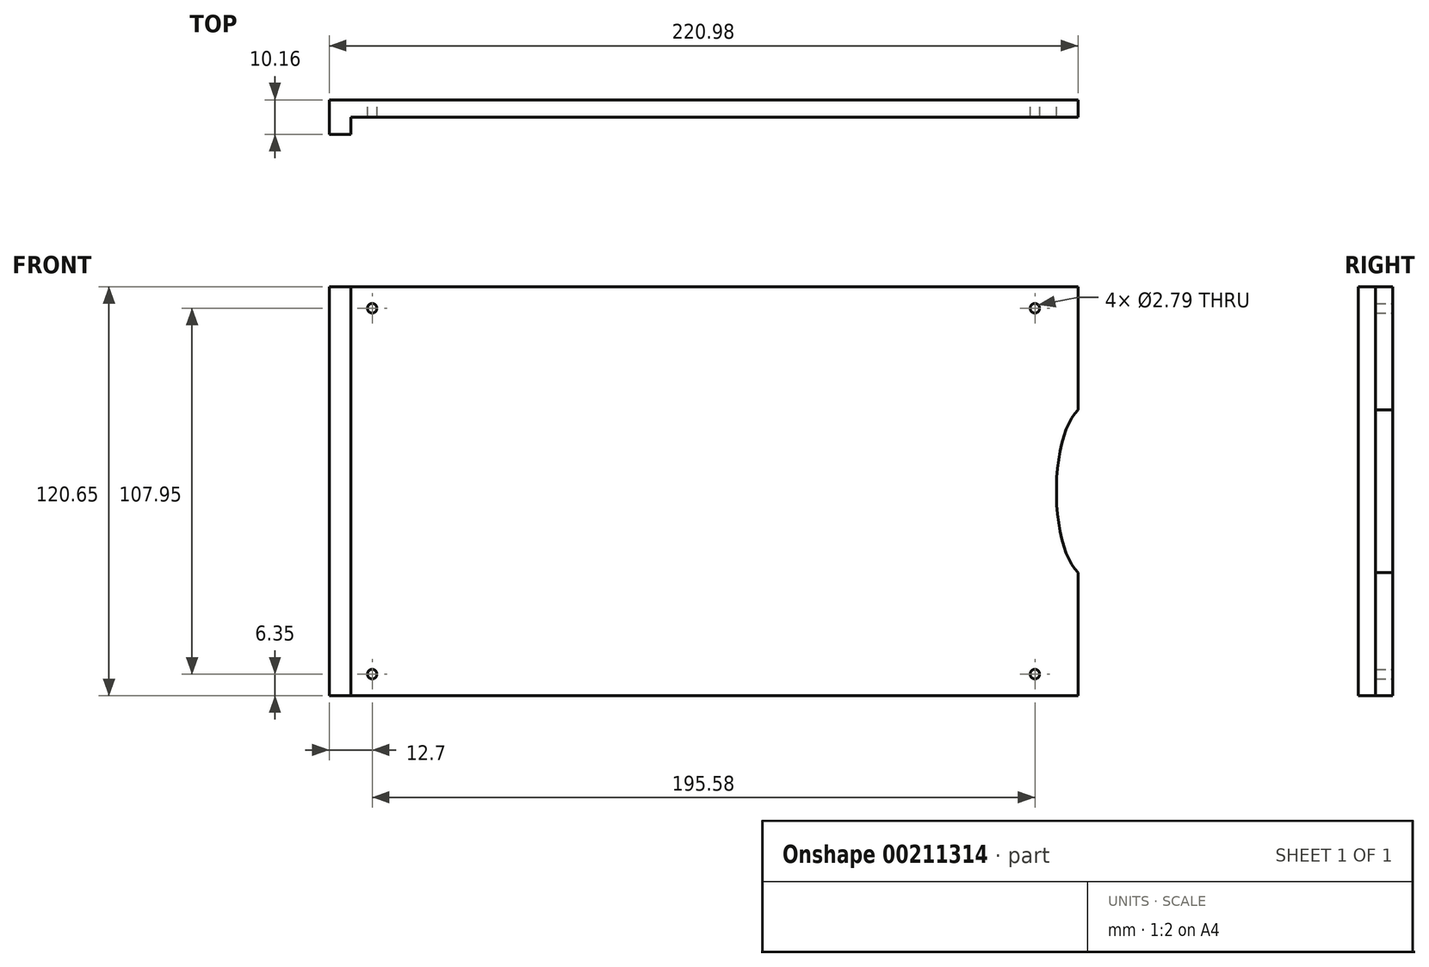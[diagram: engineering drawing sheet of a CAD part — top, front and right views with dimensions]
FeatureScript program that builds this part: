
annotation { "Feature Type Name" : "Feature", "Feature Type Description" : "" }
export const myFeature = defineFeature(function(context is Context, id is Id, definition is map)
    precondition{}
    {
        {
            var Q0;
            Q0=qCreatedBy(makeId("Front.planeOp"),FACE);
            var sketch = newSketch(context, id + "F0", { "sketchPlane" : qUnion([Q0])});
            skLineSegment(sketch, "E0.bottom", {"start": v(0, 0) * mm, "end": v(220.98, 0) * mm});
            skLineSegment(sketch, "E0.top", {"start": v(0, 120.65) * mm, "end": v(220.98, 120.65) * mm});
            skLineSegment(sketch, "E0.left", {"start": v(0, 0) * mm, "end": v(0, 120.65) * mm});
            skLineSegment(sketch, "E0.right", {"start": v(220.98, 0) * mm, "end": v(220.98, 120.65) * mm});
            skCircle(sketch, "E1", {"center": v(12.7, 114.3) * mm, "radius": 1.4 * mm});
            skCircle(sketch, "E2", {"center": v(12.7, 6.35) * mm, "radius": 1.4 * mm});
            skCircle(sketch, "E3", {"center": v(208.28, 6.35) * mm, "radius": 1.4 * mm});
            skCircle(sketch, "E4", {"center": v(208.28, 114.3) * mm, "radius": 1.4 * mm});
            skSolve(sketch);
        }
        {
            var Q0;
            Q0=makeQuery(id+"F0.imprint","IMPRINT",FACE,{"disambiguationData":[TD([[makeQuery(id+"F0.imprint","IMPRINT",EDGE,{"derivedFrom":sQuery(id+"F0.wireOp",EDGE,"E0.bottom")}),1.0]])]});
            extrude(context, id + "F1", {"entities" : qUnion([Q0]), "depth" : 5.08 * mm});
        }
        {
            var Q0;
            Q0=makeQuery(id+"F1.opExtrude","CAP_FACE",FACE,{"disambiguationData":[OSD([sQuery(id+"F0.wireOp",EDGE,"E0.bottom"),sQuery(id+"F0.wireOp",EDGE,"E0.top"),sQuery(id+"F0.wireOp",EDGE,"E0.left"),sQuery(id+"F0.wireOp",EDGE,"E0.right"),sQuery(id+"F0.wireOp",EDGE,"E1"),sQuery(id+"F0.wireOp",EDGE,"E2"),sQuery(id+"F0.wireOp",EDGE,"E3"),sQuery(id+"F0.wireOp",EDGE,"E4")])],"isStart":false});
            var sketch = newSketch(context, id + "F2", { "sketchPlane" : qUnion([Q0])});
            skLineSegment(sketch, "E5.bottom", {"start": v(0, 0) * mm, "end": v(220.98, 0) * mm});
            skLineSegment(sketch, "E5.top", {"start": v(0, 12.7) * mm, "end": v(220.98, 12.7) * mm});
            skLineSegment(sketch, "E5.left", {"start": v(0, 0) * mm, "end": v(0, 12.7) * mm});
            skLineSegment(sketch, "E5.right", {"start": v(220.98, 0) * mm, "end": v(220.98, 12.7) * mm});
            skLineSegment(sketch, "E6.bottom", {"start": v(220.98, 120.65) * mm, "end": v(0, 120.65) * mm});
            skLineSegment(sketch, "E6.top", {"start": v(220.98, 107.95) * mm, "end": v(0, 107.95) * mm});
            skLineSegment(sketch, "E6.left", {"start": v(220.98, 120.65) * mm, "end": v(220.98, 107.95) * mm});
            skLineSegment(sketch, "E6.right", {"start": v(0, 120.65) * mm, "end": v(0, 107.95) * mm});
            skLineSegment(sketch, "E7.bottom", {"start": v(0, 120.65) * mm, "end": v(6.35, 120.65) * mm});
            skLineSegment(sketch, "E7.top", {"start": v(0, 0) * mm, "end": v(6.35, 0) * mm});
            skLineSegment(sketch, "E7.left", {"start": v(0, 120.65) * mm, "end": v(0, 0) * mm});
            skLineSegment(sketch, "E7.right", {"start": v(6.35, 120.65) * mm, "end": v(6.35, 0) * mm});
            skSolve(sketch);
        }
        {
            var Q0;
            Q0=makeQuery(id+"F2.imprint","IMPRINT",FACE,{"disambiguationData":[TD([[makeQuery(id+"F2.imprint","IMPRINT",EDGE,{"derivedFrom":sQuery(id+"F2.wireOp",EDGE,"E6.bottom")}),-1.0]])]});
            var Q1;
            {var subQ1=makeQuery(id+"F1.opExtrude","CAP_EDGE",EDGE,{"disambiguationData":[OSD([sQuery(id+"F0.wireOp",EDGE,"E0.left")])],"isStart":false});var subQ3=sQuery(id+"F2.wireOp",EDGE,"nmPhpkej-twjM-OrHZ-VelI-oPTya3EY5Sfu");var subQ5=makeQuery(id+"F2.imprint","INTERSECT",VERTEX,{"derivedFrom":[subQ1,subQ3]});Q1=makeQuery(id+"F2.imprint","IMPRINT",FACE,{"disambiguationData":[TD([[makeQuery(id+"F2.imprint","IMPRINT",EDGE,{"disambiguationData":[TD([[subQ5,1.0]])],"derivedFrom":subQ3}),-1.0]])]});}
            var Q2;
            {var subQ1=makeQuery(id+"F1.opExtrude","CAP_EDGE",EDGE,{"disambiguationData":[OSD([sQuery(id+"F0.wireOp",EDGE,"E0.left")])],"isStart":false});var subQ3=sQuery(id+"F2.wireOp",EDGE,"qYEbC65u-iCHx-XNyl-o32S-FKil5MTsvIfG");var subQ5=makeQuery(id+"F2.imprint","INTERSECT",VERTEX,{"derivedFrom":[subQ1,subQ3]});Q2=makeQuery(id+"F2.imprint","IMPRINT",FACE,{"disambiguationData":[TD([[makeQuery(id+"F2.imprint","IMPRINT",EDGE,{"disambiguationData":[TD([[subQ5,1.0]])],"derivedFrom":subQ3}),1.0]])]});}
            var Q3;
            Q3=makeQuery(id+"F2.imprint","IMPRINT",FACE,{"disambiguationData":[TD([[makeQuery(id+"F2.imprint","IMPRINT",EDGE,{"derivedFrom":sQuery(id+"F2.wireOp",EDGE,"E5.bottom")}),1.0]])]});
            var Q4;
            {var subQ0=sQuery(id+"F2.wireOp",EDGE,"E7.left");var subQ1=sQuery(id+"F2.wireOp",EDGE,"E5.top");var subQ2=makeQuery(id+"F2.imprint","INTERSECT",VERTEX,{"derivedFrom":[subQ1,subQ0]});Q4=makeQuery(id+"F2.imprint","IMPRINT",FACE,{"disambiguationData":[TD([[makeQuery(id+"F2.imprint","IMPRINT",EDGE,{"disambiguationData":[TD([[subQ2,-1.0]])],"derivedFrom":subQ1}),1.0]])]});}
            var Q5;
            {var subQ5=sQuery(id+"F2.wireOp",EDGE,"E7.bottom");Q5=makeQuery(id+"F2.imprint","IMPRINT",FACE,{"disambiguationData":[TD([[makeQuery(id+"F2.imprint","IMPRINT",EDGE,{"derivedFrom":subQ5}),-1.0]])]});}
            var Q6;
            {var subQ5=sQuery(id+"F2.wireOp",EDGE,"E7.top");Q6=makeQuery(id+"F2.imprint","IMPRINT",FACE,{"disambiguationData":[TD([[makeQuery(id+"F2.imprint","IMPRINT",EDGE,{"derivedFrom":subQ5}),1.0]])]});}
            extrude(context, id + "F3", {"entities" : qUnion([Q0, Q1, Q2, Q3, Q4, Q5, Q6]), "operationType" : NewBodyOperationType.ADD, "depth" : 5.08 * mm});
        }
        {
            var Q0;
            Q0=makeQuery(id+"F1.opExtrude","CAP_FACE",FACE,{"disambiguationData":[OSD([sQuery(id+"F0.wireOp",EDGE,"E0.bottom"),sQuery(id+"F0.wireOp",EDGE,"E0.top"),sQuery(id+"F0.wireOp",EDGE,"E0.left"),sQuery(id+"F0.wireOp",EDGE,"E0.right"),sQuery(id+"F0.wireOp",EDGE,"E1"),sQuery(id+"F0.wireOp",EDGE,"E2"),sQuery(id+"F0.wireOp",EDGE,"E3"),sQuery(id+"F0.wireOp",EDGE,"E4")])],"isStart":false});
            var sketch = newSketch(context, id + "F4", { "sketchPlane" : qUnion([Q0])});
            skEllipse(sketch, "E8", {"center": v(224.16, 60.32) * mm, "majorRadius": 25.4 * mm, "minorRadius": 9.53 * mm, "majorAxis": v(0, 1)});
            skSolve(sketch);
        }
        {
            var Q0;
            Q0 = qSketchRegion(id + "F4", true);
            extrude(context, id + "F5", {"entities" : qUnion([Q0]), "operationType" : NewBodyOperationType.REMOVE, "oppositeDirection" : true, "depth" : 25.4 * mm});
        }
    });
